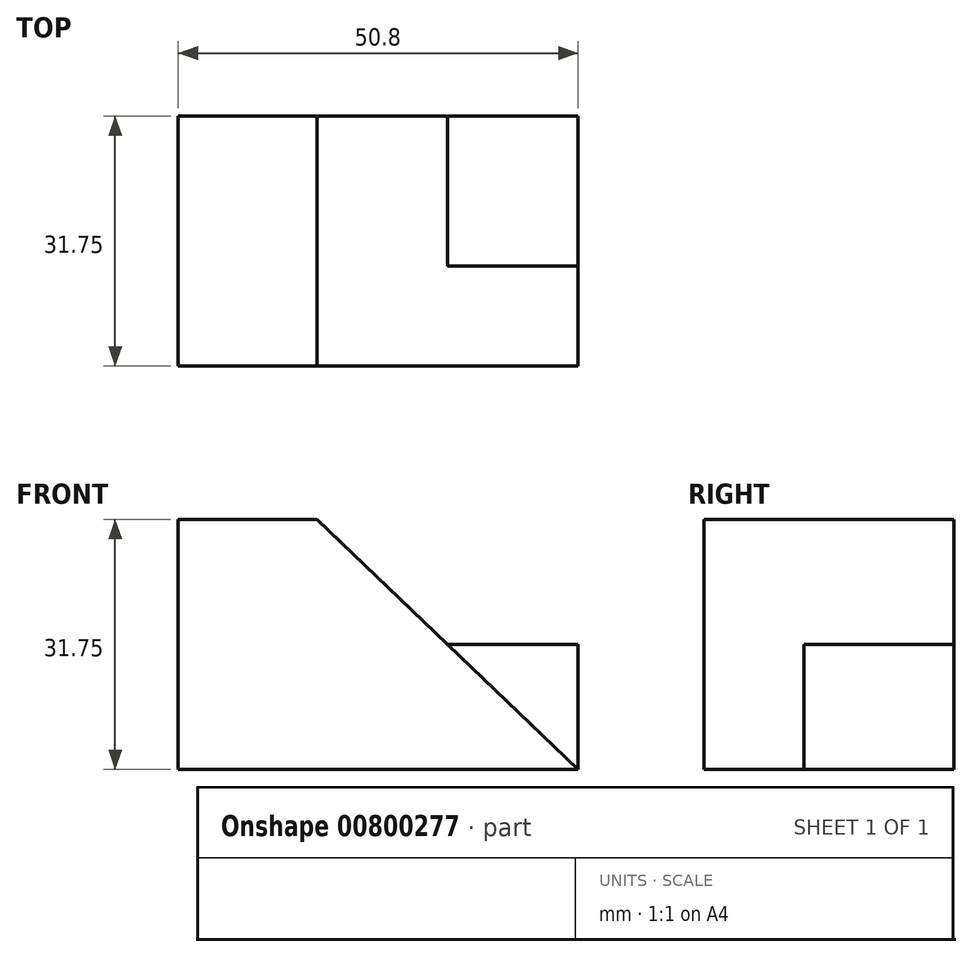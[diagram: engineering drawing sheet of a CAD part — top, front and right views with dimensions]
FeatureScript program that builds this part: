
annotation { "Feature Type Name" : "Feature", "Feature Type Description" : "" }
export const myFeature = defineFeature(function(context is Context, id is Id, definition is map)
    precondition{}
    {
        {
            var Q0;
            Q0=qCreatedBy(makeId("Front.planeOp"),FACE);
            var sketch = newSketch(context, id + "F0", { "sketchPlane" : qUnion([Q0])});
            skLineSegment(sketch, "E0", {"start": v(0, 0) * mm, "end": v(50.8, 0) * mm});
            skLineSegment(sketch, "E1", {"start": v(50.8, 0) * mm, "end": v(50.8, 31.75) * mm});
            skLineSegment(sketch, "E2", {"start": v(50.8, 31.75) * mm, "end": v(0, 31.75) * mm});
            skLineSegment(sketch, "E3", {"start": v(0, 31.75) * mm, "end": v(0, 0) * mm});
            skSolve(sketch);
        }
        {
            var Q0;
            Q0=makeQuery(id+"F0.imprint","IMPRINT",FACE,{"disambiguationData":[TD([[makeQuery(id+"F0.imprint","IMPRINT",EDGE,{"derivedFrom":sQuery(id+"F0.wireOp",EDGE,"E0")}),1.0]])]});
            extrude(context, id + "F1", {"entities" : qUnion([Q0]), "depth" : 31.75 * mm});
        }
        {
            var Q0;
            Q0=makeQuery(id+"F1.opExtrude","CAP_FACE",FACE,{"disambiguationData":[OSD([sQuery(id+"F0.wireOp",EDGE,"E0"),sQuery(id+"F0.wireOp",EDGE,"E1"),sQuery(id+"F0.wireOp",EDGE,"E2"),sQuery(id+"F0.wireOp",EDGE,"E3")])],"isStart":false});
            var sketch = newSketch(context, id + "F2", { "sketchPlane" : qUnion([Q0])});
            skLineSegment(sketch, "E4", {"start": v(17.64, 31.75) * mm, "end": v(50.8, 0) * mm});
            skSolve(sketch);
        }
        {
            var Q0;
            Q0=qSketchRegion(id+"F2",true);
            var Q1;
            {var subQ0=sQuery(id+"F2.wireOp",EDGE,"E4");Q1=makeQuery(id+"F2.imprint","IMPRINT",FACE,{"disambiguationData":[TD([[makeQuery(id+"F2.imprint","IMPRINT",EDGE,{"derivedFrom":subQ0}),1.0]])]});}
            extrude(context, id + "F3", {"entities" : qUnion([Q0, Q1]), "operationType" : NewBodyOperationType.REMOVE, "oppositeDirection" : true, "depth" : 12.7 * mm});
        }
        {
            var Q0;
            Q0=makeQuery(id+"F3.boolean.opBoolean","COPY",FACE,{"derivedFrom":makeQuery(id+"F3.opExtrude","CAP_FACE",FACE,{"disambiguationData":[OSD([sQuery(id+"F0.wireOp",EDGE,"E1"),sQuery(id+"F0.wireOp",EDGE,"E2"),sQuery(id+"F2.wireOp",EDGE,"E4")])],"isStart":false})});
            var sketch = newSketch(context, id + "F4", { "sketchPlane" : qUnion([Q0])});
            skLineSegment(sketch, "E5", {"start": v(34.22, 15.87) * mm, "end": v(34.22, 31.75) * mm});
            skSolve(sketch);
        }
        {
            var Q0;
            Q0=qSketchRegion(id+"F4",true);
            var Q1;
            {var subQ0=sQuery(id+"F4.wireOp",EDGE,"E5");Q1=makeQuery(id+"F4.imprint","IMPRINT",FACE,{"disambiguationData":[TD([[makeQuery(id+"F4.imprint","IMPRINT",EDGE,{"derivedFrom":subQ0}),1.0]])]});}
            extrude(context, id + "F5", {"entities" : qUnion([Q0, Q1]), "operationType" : NewBodyOperationType.REMOVE, "oppositeDirection" : true, "depth" : 25.4 * mm});
        }
        {
            var Q0;
            Q0=makeQuery(id+"F3.boolean.opBoolean","COPY",FACE,{"derivedFrom":makeQuery(id+"F3.opExtrude","CAP_FACE",FACE,{"disambiguationData":[OSD([sQuery(id+"F0.wireOp",EDGE,"E1"),sQuery(id+"F0.wireOp",EDGE,"E2"),sQuery(id+"F2.wireOp",EDGE,"E4")])],"isStart":false})});
            var sketch = newSketch(context, id + "F6", { "sketchPlane" : qUnion([Q0])});
            skLineSegment(sketch, "E6", {"start": v(34.22, 23.81) * mm, "end": v(50.8, 23.81) * mm});
            skLineSegment(sketch, "E7", {"start": v(50.8, 23.81) * mm, "end": v(63.04, 31.75) * mm});
            skSolve(sketch);
        }
        {
            var Q0;
            Q0=qSketchRegion(id+"F6",true);
            var Q1;
            {var subQ0=sQuery(id+"F6.wireOp",EDGE,"E6");Q1=makeQuery(id+"F6.imprint","IMPRINT",FACE,{"disambiguationData":[TD([[makeQuery(id+"F6.imprint","IMPRINT",EDGE,{"derivedFrom":subQ0}),1.0]])]});}
            extrude(context, id + "F7", {"entities" : qUnion([Q0, Q1]), "operationType" : NewBodyOperationType.REMOVE, "oppositeDirection" : true, "depth" : 25.4 * mm});
        }
        {
            var Q0;
            Q0=makeQuery(id+"F3.boolean.opBoolean","COPY",FACE,{"derivedFrom":makeQuery(id+"F3.opExtrude","CAP_FACE",FACE,{"disambiguationData":[OSD([sQuery(id+"F0.wireOp",EDGE,"E1"),sQuery(id+"F0.wireOp",EDGE,"E2"),sQuery(id+"F2.wireOp",EDGE,"E4")])],"isStart":false})});
            var sketch = newSketch(context, id + "F8", { "sketchPlane" : qUnion([Q0])});
            skLineSegment(sketch, "E8", {"start": v(34.22, 15.88) * mm, "end": v(50.8, 15.88) * mm});
            skLineSegment(sketch, "E9", {"start": v(50.8, 15.88) * mm, "end": v(63.6, 23.81) * mm});
            skSolve(sketch);
        }
        {
            var Q0;
            Q0=qSketchRegion(id+"F8",true);
            var Q1;
            {var subQ0=sQuery(id+"F8.wireOp",EDGE,"E8");Q1=makeQuery(id+"F8.imprint","IMPRINT",FACE,{"disambiguationData":[TD([[makeQuery(id+"F8.imprint","IMPRINT",EDGE,{"derivedFrom":subQ0}),1.0]])]});}
            extrude(context, id + "F9", {"entities" : qUnion([Q0, Q1]), "operationType" : NewBodyOperationType.REMOVE, "oppositeDirection" : true, "depth" : 25.4 * mm});
        }
    });
